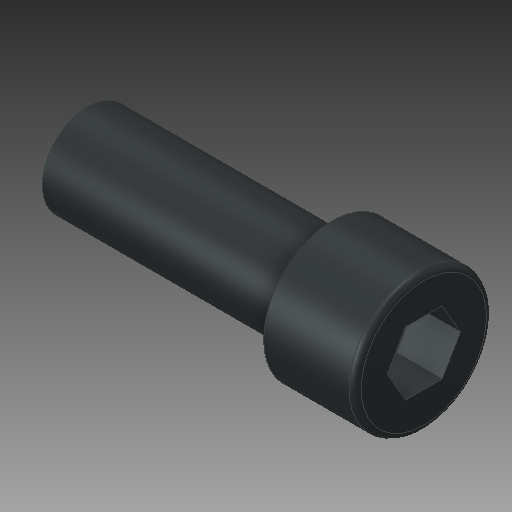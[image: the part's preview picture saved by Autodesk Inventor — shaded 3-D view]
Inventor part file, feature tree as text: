
AUTODESK INVENTOR PART (.ipt)
format: ipt  version: 2019 (Build 230136000, 136)  size: 137,728 bytes
history: native  units: mm
features: extrude x3, sketch x3, plane x1, fillet x1
ambient origin geometry x8: Origin, YZ Plane, XZ Plane, XY Plane, X Axis, Y Axis, Z Axis, Center Point
bodies: Solid1 (feature_tree)
feature tree (8):
  extrude  "Extrusion1"  Depth=8.0mm TaperAngle=0.0deg
  extrude  "Extrusion2"  Depth=3.0mm TaperAngle=0.0deg
  plane  "Work Plane1"
  fillet  "Fillet2"  Radius=0.2mm
  extrude  "Extrusion4"  Depth=1.5mm
  sketch  "Sketch1"  dims[d0=3.0mm d1=8.0mm d2=0.0mm]
  sketch  "Sketch2"  dims[d3=4.5mm d4=3.0mm d5=0.0mm d13=0.2mm]
  sketch  "Sketch4"  dims[d14=2.4mm d15=1.03923mm d16=1.5mm d17=0.0mm]
